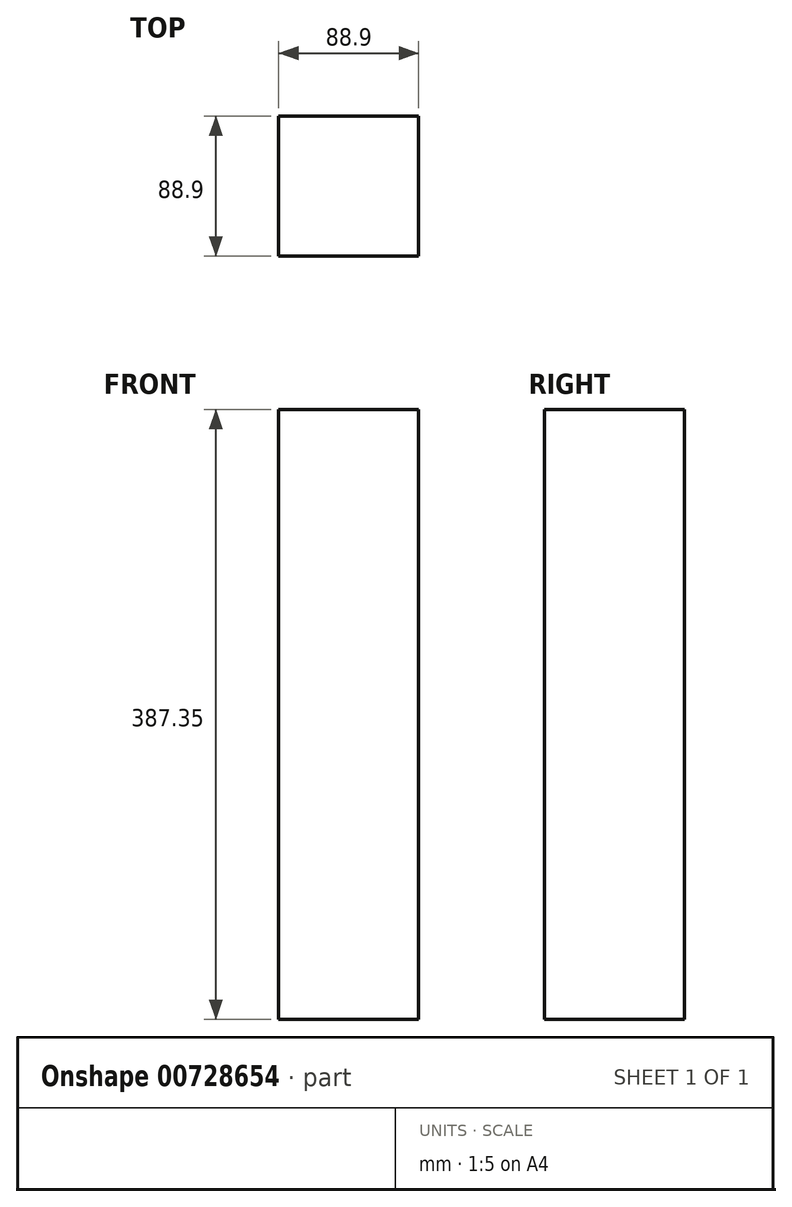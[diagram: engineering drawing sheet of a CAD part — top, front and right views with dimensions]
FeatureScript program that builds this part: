
annotation { "Feature Type Name" : "Feature", "Feature Type Description" : "" }
export const myFeature = defineFeature(function(context is Context, id is Id, definition is map)
    precondition{}
    {
        {
            var Q0;
            Q0=qCreatedBy(makeId("Top.planeOp"),FACE);
            var sketch = newSketch(context, id + "F0", { "sketchPlane" : qUnion([Q0])});
            skLineSegment(sketch, "E0.bottom", {"start": v(44.45, 44.45) * mm, "end": v(-44.45, 44.45) * mm});
            skLineSegment(sketch, "E0.top", {"start": v(44.45, -44.45) * mm, "end": v(-44.45, -44.45) * mm});
            skLineSegment(sketch, "E0.left", {"start": v(44.45, 44.45) * mm, "end": v(44.45, -44.45) * mm});
            skLineSegment(sketch, "E0.right", {"start": v(-44.45, 44.45) * mm, "end": v(-44.45, -44.45) * mm});
            skPoint(sketch, "E0.middle", {"position": v(0, 0) * mm});
            skSolve(sketch);
        }
        {
            var Q0;
            Q0 = qSketchRegion(id + "F0", true);
            extrude(context, id + "F1", {"entities" : qUnion([Q0]), "depth" : 387.35 * mm, "offsetDistance" : 25.4 * mm});
        }
    });
